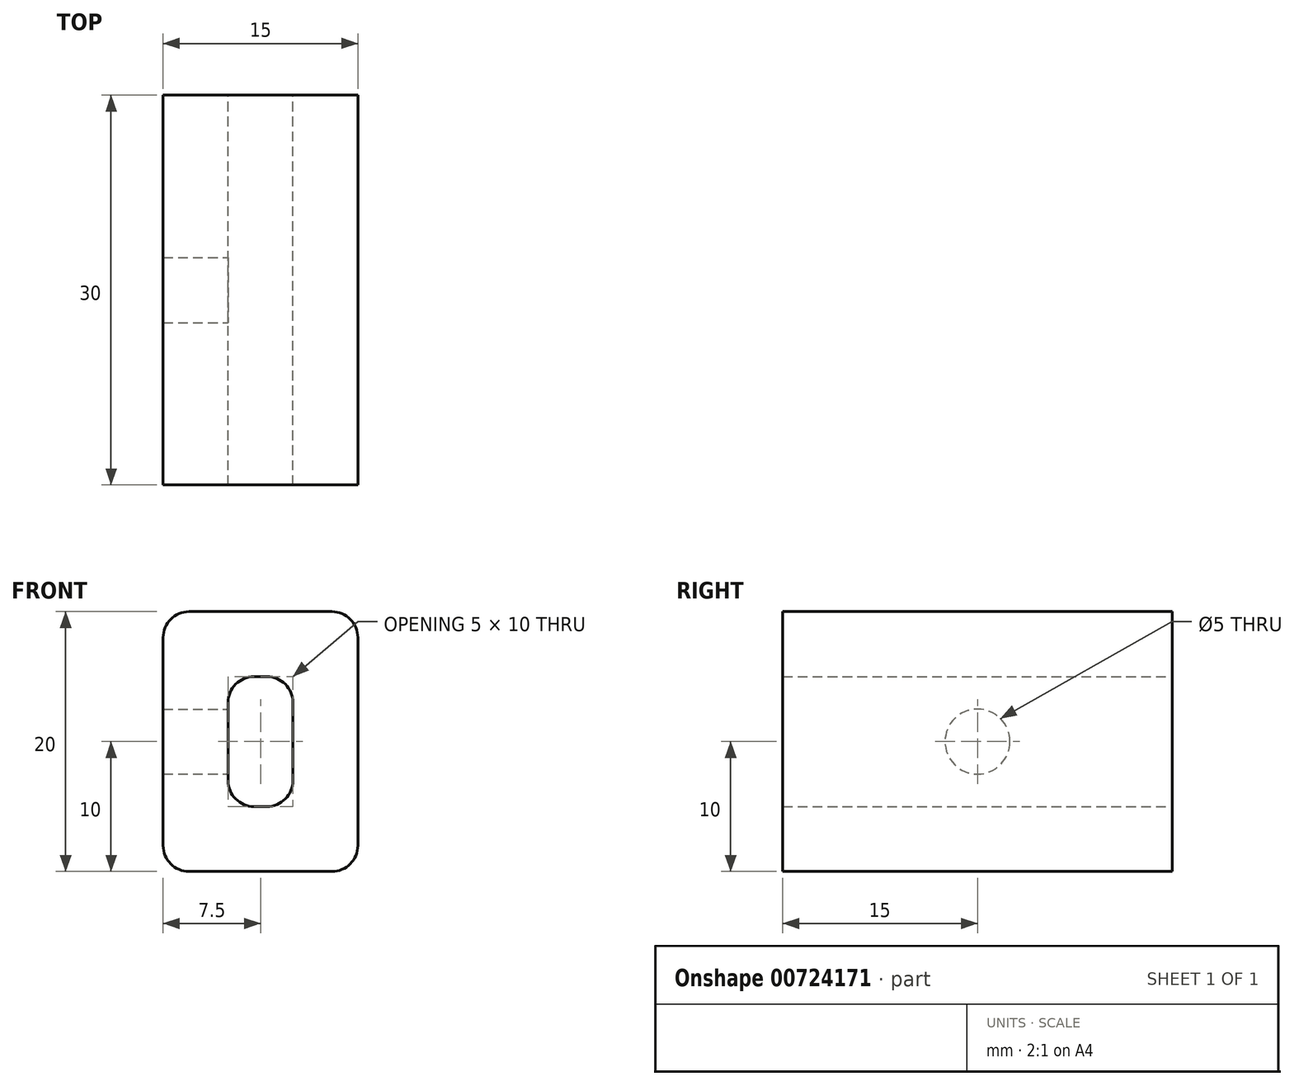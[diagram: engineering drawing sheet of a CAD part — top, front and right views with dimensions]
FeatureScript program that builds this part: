
annotation { "Feature Type Name" : "Feature", "Feature Type Description" : "" }
export const myFeature = defineFeature(function(context is Context, id is Id, definition is map)
    precondition{}
    {
        {
            var Q0;
            Q0=qCreatedBy(makeId("Front.planeOp"),FACE);
            var sketch = newSketch(context, id + "F0", { "sketchPlane" : qUnion([Q0])});
            skLineSegment(sketch, "E0.bottom", {"start": v(0.5, 5) * mm, "end": v(-0.5, 5) * mm});
            skLineSegment(sketch, "E0.top", {"start": v(0.5, -5) * mm, "end": v(-0.5, -5) * mm});
            skLineSegment(sketch, "E0.left", {"start": v(2.5, 3) * mm, "end": v(2.5, -3) * mm});
            skLineSegment(sketch, "E0.right", {"start": v(-2.5, 3) * mm, "end": v(-2.5, -3) * mm});
            skPoint(sketch, "E0.middle", {"position": v(0, 0) * mm});
            skLineSegment(sketch, "E1.bottom", {"start": v(5.5, 10) * mm, "end": v(-5.5, 10) * mm});
            skLineSegment(sketch, "E1.top", {"start": v(5.5, -10) * mm, "end": v(-5.5, -10) * mm});
            skLineSegment(sketch, "E1.left", {"start": v(7.5, 8) * mm, "end": v(7.5, -8) * mm});
            skLineSegment(sketch, "E1.right", {"start": v(-7.5, 8) * mm, "end": v(-7.5, -8) * mm});
            skPoint(sketch, "E2.visualSharp", {"position": v(-7.5, 10) * mm});
            skArc(sketch, "E2.filletArc", {"start": v(-5.5, 10) * mm, "mid": v(-6.91, 9.41) * mm, "end": v(-7.5, 8) * mm});
            skPoint(sketch, "E3.visualSharp", {"position": v(7.5, 10) * mm});
            skArc(sketch, "E3.filletArc", {"start": v(7.5, 8) * mm, "mid": v(6.91, 9.41) * mm, "end": v(5.5, 10) * mm});
            skPoint(sketch, "E4.visualSharp", {"position": v(7.5, -10) * mm});
            skArc(sketch, "E4.filletArc", {"start": v(5.5, -10) * mm, "mid": v(6.91, -9.41) * mm, "end": v(7.5, -8) * mm});
            skPoint(sketch, "E5.visualSharp", {"position": v(-7.5, -10) * mm});
            skArc(sketch, "E5.filletArc", {"start": v(-7.5, -8) * mm, "mid": v(-6.91, -9.41) * mm, "end": v(-5.5, -10) * mm});
            skPoint(sketch, "E6.visualSharp", {"position": v(-2.5, 5) * mm});
            skArc(sketch, "E6.filletArc", {"start": v(-0.5, 5) * mm, "mid": v(-1.91, 4.41) * mm, "end": v(-2.5, 3) * mm});
            skPoint(sketch, "E7.visualSharp", {"position": v(-2.5, -5) * mm});
            skArc(sketch, "E7.filletArc", {"start": v(-2.5, -3) * mm, "mid": v(-1.91, -4.41) * mm, "end": v(-0.5, -5) * mm});
            skPoint(sketch, "E8.visualSharp", {"position": v(2.5, -5) * mm});
            skArc(sketch, "E8.filletArc", {"start": v(0.5, -5) * mm, "mid": v(1.91, -4.41) * mm, "end": v(2.5, -3) * mm});
            skPoint(sketch, "E9.visualSharp", {"position": v(2.5, 5) * mm});
            skArc(sketch, "E9.filletArc", {"start": v(2.5, 3) * mm, "mid": v(1.91, 4.41) * mm, "end": v(0.5, 5) * mm});
            skSolve(sketch);
        }
        {
            var Q0;
            Q0 = qSketchRegion(id + "F0", true);
            extrude(context, id + "F1", {"entities" : qUnion([Q0]), "depth" : 30 * mm, "offsetDistance" : 25 * mm});
        }
        {
            var Q0;
            Q0=qCreatedBy(makeId("Right.planeOp"),FACE);
            var sketch = newSketch(context, id + "F2", { "sketchPlane" : qUnion([Q0])});
            skCircle(sketch, "E10", {"center": v(-15, 0) * mm, "radius": 2.5 * mm});
            skSolve(sketch);
        }
        {
            var Q0;
            Q0 = qSketchRegion(id + "F2", true);
            extrude(context, id + "F3", {"entities" : qUnion([Q0]), "operationType" : NewBodyOperationType.REMOVE, "oppositeDirection" : true, "depth" : 30 * mm, "offsetDistance" : 25 * mm});
        }
    });
